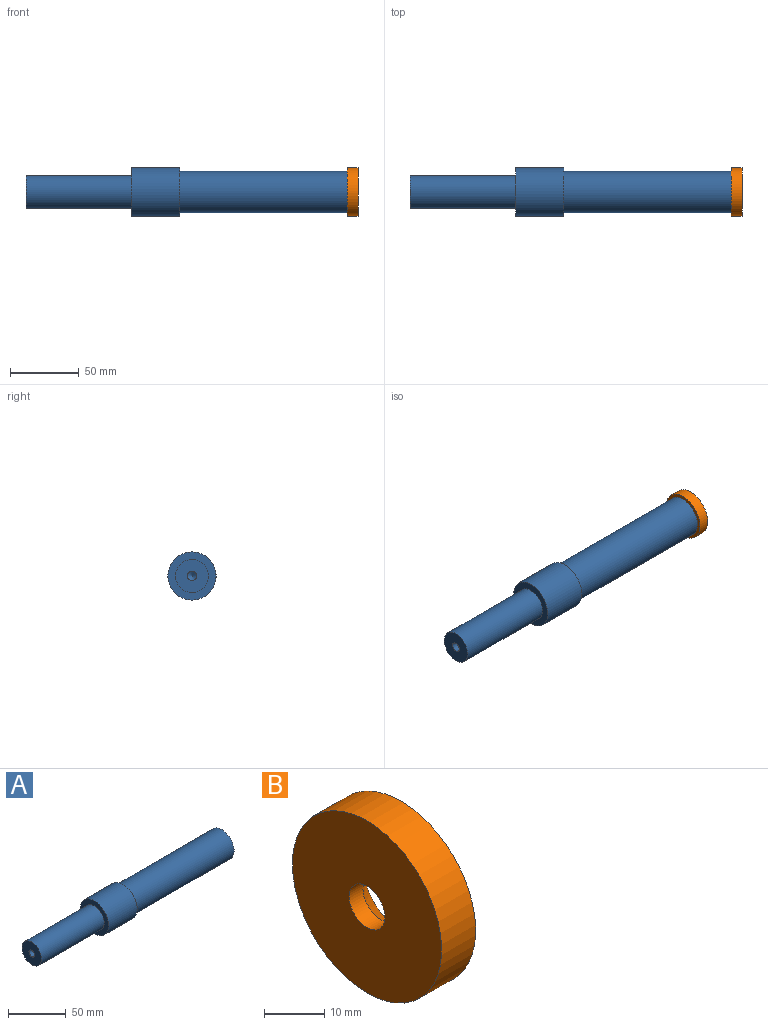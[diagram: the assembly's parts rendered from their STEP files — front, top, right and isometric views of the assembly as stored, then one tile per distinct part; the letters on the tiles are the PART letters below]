
ASSEMBLY  parts=2 mates=1
PART A: 11 faces, bbox 233.5x35x35 mm
  f0: plane 35x35mm, normal (-1,0,0), area 509.7mm2, adj f1,f5
  f1: cylinder r=12mm len=77mm, axis (1,0,0), area 5805.7mm2, adj f0,f2
  f2: plane 24x24mm, normal (-1,0,0), area 416.1mm2, adj f1,f3
  f3: cylinder r=3.4mm len=30mm, axis (-1,0,0), area 640.9mm2, adj f2,f4
  f4: cone r=0mm half-angle=59deg, axis (-1,0,0), area 42.4mm2, adj f3
  f5: cylinder r=17.5mm len=35mm, axis (-1,0,0), area 3848.5mm2, adj f0,f6
  f6: plane 35x35mm, normal (1,0,0), area 255.3mm2, adj f5,f8
  f7: plane 30x30mm, normal (1,0,0), area 670.5mm2, adj f8,f9
  f8: cylinder r=15mm len=121.5mm, axis (1,0,0), area 11451.1mm2, adj f6,f7
  f9: cylinder r=3.4mm len=30mm, axis (1,0,0), area 640.9mm2, adj f7,f10
  f10: cone r=0mm half-angle=59deg, axis (1,0,0), area 42.4mm2, adj f9
PART B: 5 faces, bbox 8x35x35 mm
  f0: cylinder r=17.5mm len=35mm, axis (-1,0,0), area 879.6mm2, adj f1,f2
  f1: plane 35x35mm, normal (1,0,0), area 709.9mm2, adj f0,f4
  f2: plane 35x35mm, normal (-1,0,0), area 906.7mm2, adj f0,f3
  f3: cylinder r=4.2mm len=8.4mm, axis (1,0,0), area 85.5mm2, adj f2,f4
  f4: cone r=4.2mm half-angle=45deg, axis (1,0,0), area 278.3mm2, adj f1,f3
PLACE A at identity
PLACE B at identity
MATE fastened B.f0 <-> A.f1  axis (-1,0,0) through (0,0,0)mm
